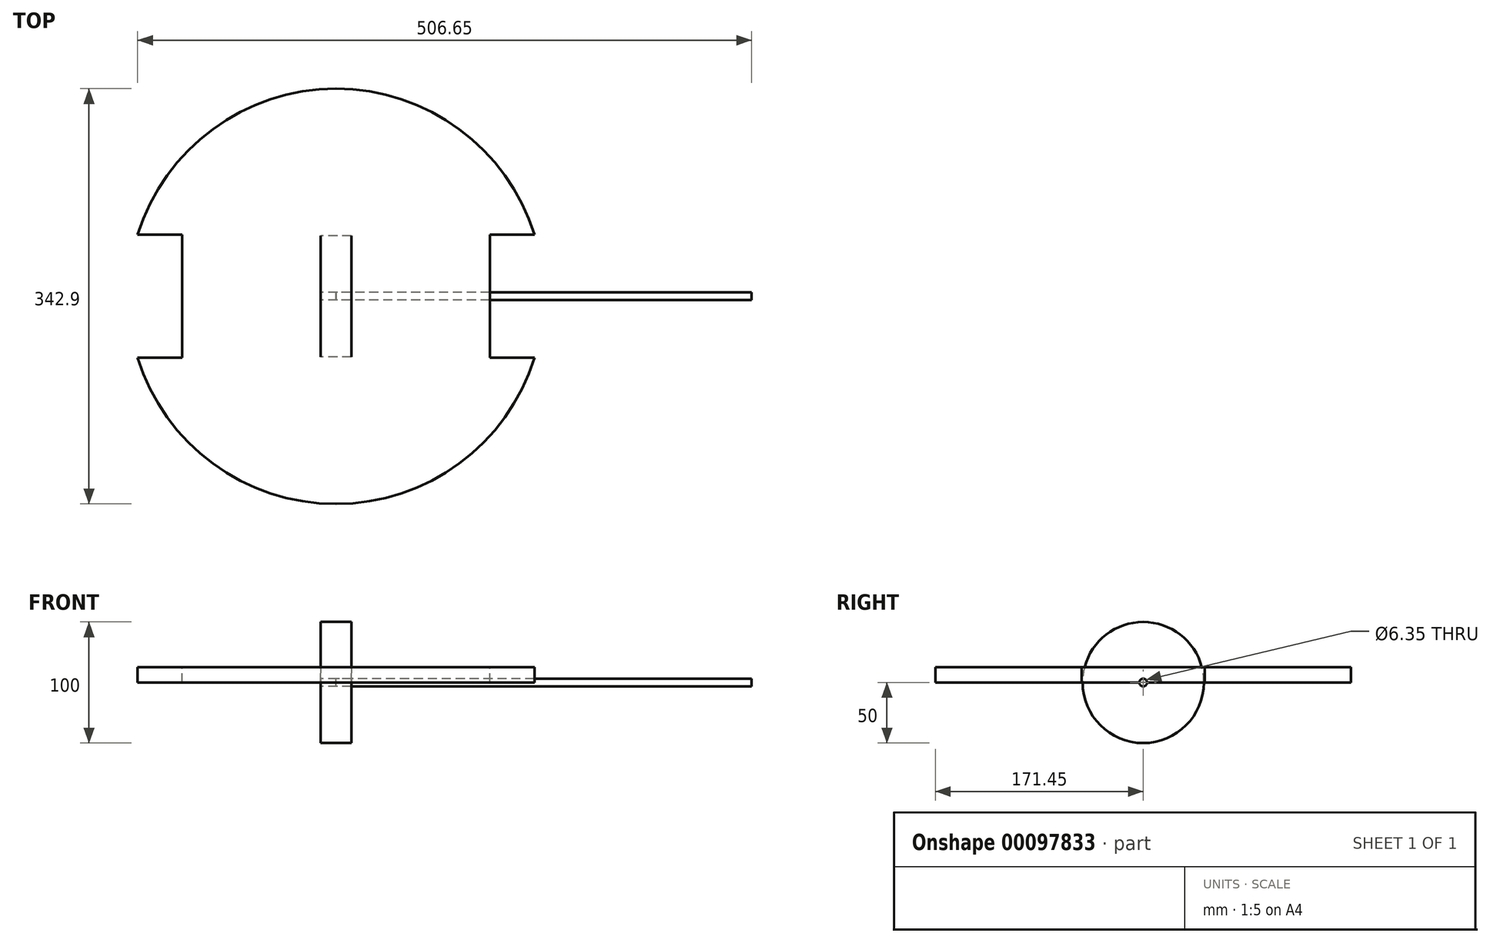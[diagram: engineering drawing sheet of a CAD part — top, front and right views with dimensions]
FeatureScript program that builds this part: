
annotation { "Feature Type Name" : "Feature", "Feature Type Description" : "" }
export const myFeature = defineFeature(function(context is Context, id is Id, definition is map)
    precondition{}
    {
        {
            var Q0;
            Q0=qCreatedBy(makeId("Top.planeOp"),FACE);
            var sketch = newSketch(context, id + "F0", { "sketchPlane" : qUnion([Q0])});
            skCircle(sketch, "E0", {"center": v(0, 0) * mm, "radius": 171.45 * mm});
            skSolve(sketch);
        }
        {
            var Q0;
            Q0=makeQuery(id+"F0.imprint","IMPRINT",FACE,{"disambiguationData":[TD([[makeQuery(id+"F0.imprint","IMPRINT",EDGE,{"derivedFrom":sQuery(id+"F0.wireOp",EDGE,"E0")}),1.0]])]});
            extrude(context, id + "F1", {"entities" : qUnion([Q0]), "depth" : 12.7 * mm});
        }
        {
            var Q0;
            Q0=makeQuery(id+"F1.opExtrude","CAP_FACE",FACE,{"disambiguationData":[OSD([sQuery(id+"F0.wireOp",EDGE,"E0")])],"isStart":false});
            var sketch = newSketch(context, id + "F2", { "sketchPlane" : qUnion([Q0])});
            skLineSegment(sketch, "E1.bottom", {"start": v(-171.45, 50.8) * mm, "end": v(-127, 50.8) * mm});
            skLineSegment(sketch, "E1.top", {"start": v(-171.45, -50.8) * mm, "end": v(-127, -50.8) * mm});
            skLineSegment(sketch, "E1.left", {"start": v(-171.45, 50.8) * mm, "end": v(-171.45, -50.8) * mm});
            skLineSegment(sketch, "E1.right", {"start": v(-127, 50.8) * mm, "end": v(-127, -50.8) * mm});
            skLineSegment(sketch, "E2.bottom", {"start": v(127, 50.8) * mm, "end": v(171.45, 50.8) * mm});
            skLineSegment(sketch, "E2.top", {"start": v(127, -50.8) * mm, "end": v(171.45, -50.8) * mm});
            skLineSegment(sketch, "E2.left", {"start": v(127, 50.8) * mm, "end": v(127, -50.8) * mm});
            skLineSegment(sketch, "E2.right", {"start": v(171.45, 50.8) * mm, "end": v(171.45, -50.8) * mm});
            skLineSegment(sketch, "E3", {"start": v(-127, 0) * mm, "end": v(127, 0) * mm, "construction": true});
            skSolve(sketch);
        }
        {
            var Q0;
            Q0 = qSketchRegion(id + "F2", true);
            extrude(context, id + "F3", {"entities" : qUnion([Q0]), "operationType" : NewBodyOperationType.REMOVE, "endBound" : BoundingType.THROUGH_ALL, "oppositeDirection" : true, "depth" : 25.4 * mm});
        }
        {
            var Q0;
            Q0=qCreatedBy(makeId("Front.planeOp"),FACE);
            var sketch = newSketch(context, id + "F4", { "sketchPlane" : qUnion([Q0])});
            skLineSegment(sketch, "E4", {"start": v(-28.5, 0) * mm, "end": v(41.57, 0) * mm, "construction": true});
            skLineSegment(sketch, "E5.bottom", {"start": v(-12.7, 50) * mm, "end": v(12.7, 50) * mm});
            skLineSegment(sketch, "E5.top", {"start": v(-12.7, 3.18) * mm, "end": v(12.7, 3.18) * mm});
            skLineSegment(sketch, "E5.left", {"start": v(-12.7, 50) * mm, "end": v(-12.7, 3.18) * mm});
            skLineSegment(sketch, "E5.right", {"start": v(12.7, 50) * mm, "end": v(12.7, 3.18) * mm});
            skLineSegment(sketch, "E6", {"start": v(0, 0) * mm, "end": v(0, 3.18) * mm, "construction": true});
            skSolve(sketch);
        }
        {
            var Q0;
            Q0 = qSketchRegion(id + "F4", true);
            var Q1;
            Q1=sQuery(id+"F4.wireOp",EDGE,"E4");
            revolve(context, id + "F5", {"entities" : qUnion([Q0]), "axis" : qUnion([Q1]), "revolveType" : RevolveType.FULL});
        }
        {
            var Q0;
            Q0=qCreatedBy(makeId("Right.planeOp"),FACE);
            var sketch = newSketch(context, id + "F6", { "sketchPlane" : qUnion([Q0])});
            skCircle(sketch, "E7", {"center": v(0, 0) * mm, "radius": 3.18 * mm});
            skSolve(sketch);
        }
        {
            var Q0;
            Q0=makeQuery(id+"F6.imprint","IMPRINT",FACE,{"disambiguationData":[TD([[makeQuery(id+"F6.imprint","IMPRINT",EDGE,{"derivedFrom":sQuery(id+"F6.wireOp",EDGE,"E7")}),1.0]])]});
            extrude(context, id + "F7", {"entities" : qUnion([Q0]), "depth" : 342.9 * mm});
        }
    });
